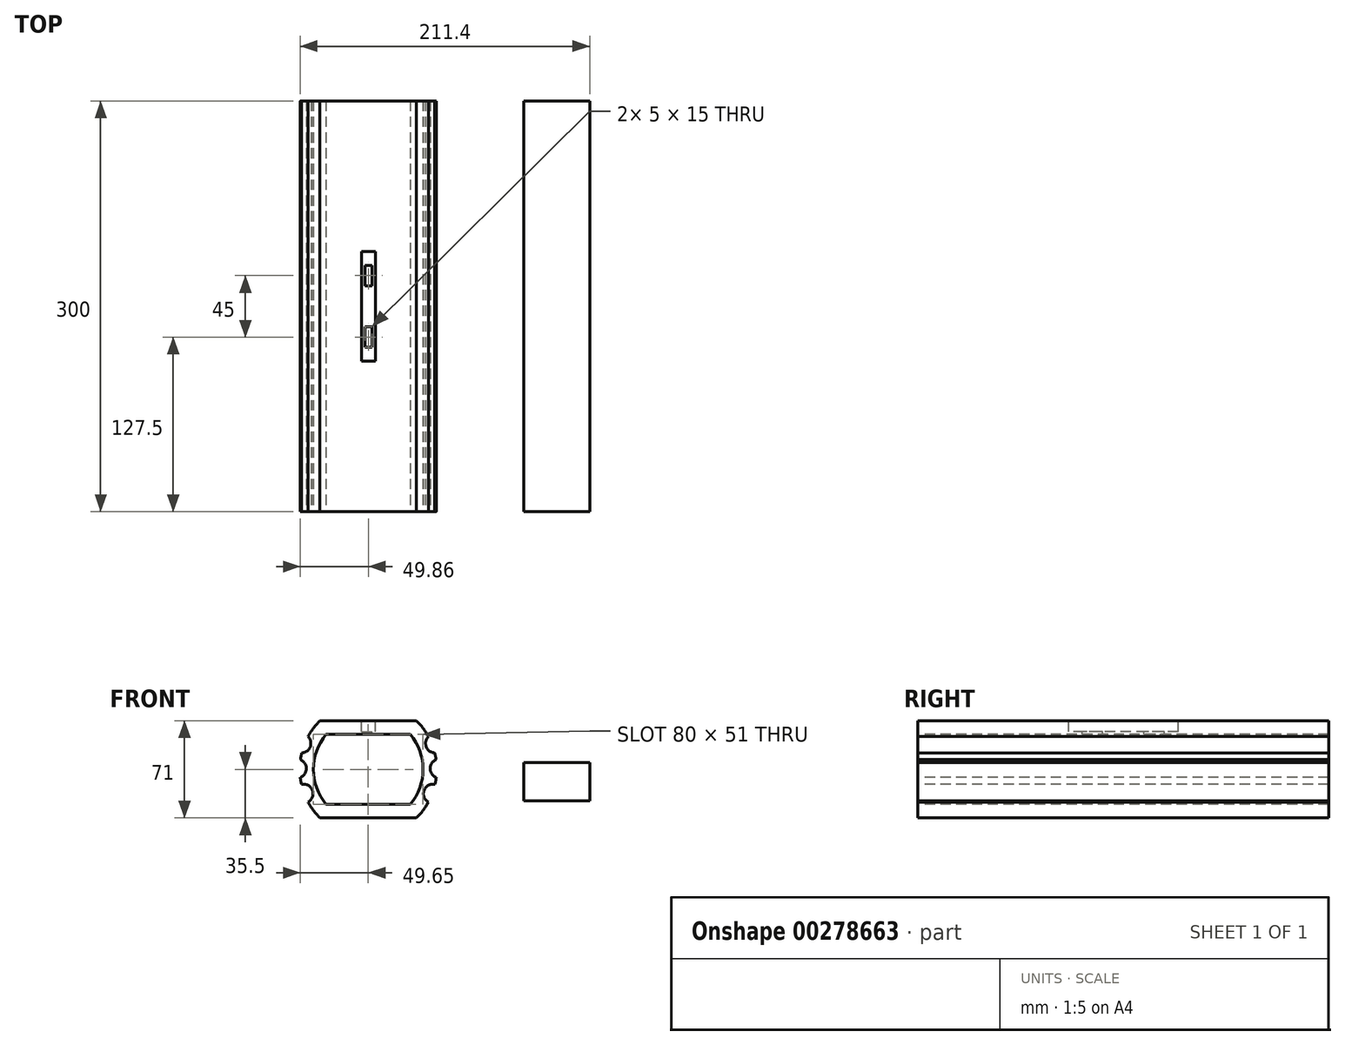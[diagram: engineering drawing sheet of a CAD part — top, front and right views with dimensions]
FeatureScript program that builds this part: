
annotation { "Feature Type Name" : "Feature", "Feature Type Description" : "" }
export const myFeature = defineFeature(function(context is Context, id is Id, definition is map)
    precondition{}
    {
        {
            var Q0;
            Q0=qCreatedBy(makeId("Front.planeOp"),FACE);
            var sketch = newSketch(context, id + "F0", { "sketchPlane" : qUnion([Q0])});
            skArc(sketch, "E0", {"start": v(-35.21, 35.5) * mm, "mid": v(-50, 0) * mm, "end": v(-35.21, -35.5) * mm});
            skLineSegment(sketch, "E1", {"start": v(-35.21, 35.5) * mm, "end": v(35.21, 35.5) * mm});
            skLineSegment(sketch, "E2", {"start": v(-35.21, -35.5) * mm, "end": v(35.21, -35.5) * mm});
            skArc(sketch, "E3.trimOffspring", {"start": v(35.21, -35.5) * mm, "mid": v(50, 0) * mm, "end": v(35.21, 35.5) * mm});
            skLineSegment(sketch, "E4.bottom", {"start": v(161.75, 4.82) * mm, "end": v(113.6, 4.82) * mm});
            skLineSegment(sketch, "E4.top", {"start": v(161.75, -22.95) * mm, "end": v(113.6, -22.95) * mm});
            skLineSegment(sketch, "E4.left", {"start": v(161.75, 4.82) * mm, "end": v(161.75, -22.95) * mm});
            skLineSegment(sketch, "E4.right", {"start": v(113.6, 4.82) * mm, "end": v(113.6, -22.95) * mm});
            skSolve(sketch);
        }
        {
            var Q0;
            Q0 = qSketchRegion(id + "F0", true);
            extrude(context, id + "F1", {"entities" : qUnion([Q0]), "depth" : 300 * mm});
        }
        {
            var Q0;
            Q0=makeQuery(id+"F1.opExtrude","CAP_FACE",FACE,{"disambiguationData":[OSD([sQuery(id+"F0.wireOp",EDGE,"E0"),sQuery(id+"F0.wireOp",EDGE,"E1"),sQuery(id+"F0.wireOp",EDGE,"E2"),sQuery(id+"F0.wireOp",EDGE,"E3.trimOffspring")])],"isStart":false});
            var sketch = newSketch(context, id + "F2", { "sketchPlane" : qUnion([Q0])});
            skArc(sketch, "E5", {"start": v(-30.82, 25.5) * mm, "mid": v(-40, 0) * mm, "end": v(-30.82, -25.5) * mm});
            skLineSegment(sketch, "E6", {"start": v(-30.82, 25.5) * mm, "end": v(30.82, 25.5) * mm});
            skLineSegment(sketch, "E7", {"start": v(-30.82, -25.5) * mm, "end": v(30.82, -25.5) * mm});
            skArc(sketch, "E8.trimOffspring", {"start": v(30.82, -25.5) * mm, "mid": v(40, 0) * mm, "end": v(30.82, 25.5) * mm});
            skSolve(sketch);
        }
        {
            var Q0;
            Q0 = qSketchRegion(id + "F2", true);
            extrude(context, id + "F3", {"entities" : qUnion([Q0]), "operationType" : NewBodyOperationType.REMOVE, "oppositeDirection" : true, "depth" : 300 * mm});
        }
        {
            var Q0;
            Q0=makeQuery(id+"F1.opExtrude","SWEPT_FACE",FACE,{"disambiguationData":[OSD([sQuery(id+"F0.wireOp",EDGE,"E1")])]});
            var sketch = newSketch(context, id + "F4", { "sketchPlane" : qUnion([Q0])});
            skLineSegment(sketch, "E9.bottom", {"start": v(-4.79, -110) * mm, "end": v(5.21, -110) * mm});
            skLineSegment(sketch, "E9.top", {"start": v(-4.79, -190) * mm, "end": v(5.21, -190) * mm});
            skLineSegment(sketch, "E9.left", {"start": v(-4.79, -110) * mm, "end": v(-4.79, -190) * mm});
            skLineSegment(sketch, "E9.right", {"start": v(5.21, -110) * mm, "end": v(5.21, -190) * mm});
            skSolve(sketch);
        }
        {
            var Q0;
            Q0 = qSketchRegion(id + "F4", true);
            extrude(context, id + "F5", {"entities" : qUnion([Q0]), "operationType" : NewBodyOperationType.REMOVE, "oppositeDirection" : true, "depth" : 8 * mm});
        }
        {
            var Q0;
            Q0=makeQuery(id+"F5.boolean.opBoolean","COPY",FACE,{"derivedFrom":makeQuery(id+"F5.opExtrude","CAP_FACE",FACE,{"disambiguationData":[OSD([sQuery(id+"F4.wireOp",EDGE,"E9.bottom"),sQuery(id+"F4.wireOp",EDGE,"E9.top"),sQuery(id+"F4.wireOp",EDGE,"E9.left"),sQuery(id+"F4.wireOp",EDGE,"E9.right")])],"isStart":false})});
            var sketch = newSketch(context, id + "F6", { "sketchPlane" : qUnion([Q0])});
            skLineSegment(sketch, "E10.bottom", {"start": v(-2.29, -120) * mm, "end": v(2.71, -120) * mm});
            skLineSegment(sketch, "E10.top", {"start": v(-2.29, -135) * mm, "end": v(2.71, -135) * mm});
            skLineSegment(sketch, "E10.left", {"start": v(-2.29, -120) * mm, "end": v(-2.29, -135) * mm});
            skLineSegment(sketch, "E10.right", {"start": v(2.71, -120) * mm, "end": v(2.71, -135) * mm});
            skLineSegment(sketch, "E11.bottom", {"start": v(-2.29, -165) * mm, "end": v(2.71, -165) * mm});
            skLineSegment(sketch, "E11.top", {"start": v(-2.29, -180) * mm, "end": v(2.71, -180) * mm});
            skLineSegment(sketch, "E11.left", {"start": v(-2.29, -165) * mm, "end": v(-2.29, -180) * mm});
            skLineSegment(sketch, "E11.right", {"start": v(2.71, -165) * mm, "end": v(2.71, -180) * mm});
            skSolve(sketch);
        }
        {
            var Q0;
            Q0 = qSketchRegion(id + "F6", true);
            extrude(context, id + "F7", {"entities" : qUnion([Q0]), "operationType" : NewBodyOperationType.REMOVE, "oppositeDirection" : true, "depth" : 5 * mm});
        }
        {
            var Q0;
            Q0=makeQuery(id+"F1.opExtrude","CAP_FACE",FACE,{"disambiguationData":[OSD([sQuery(id+"F0.wireOp",EDGE,"E0"),sQuery(id+"F0.wireOp",EDGE,"E1"),sQuery(id+"F0.wireOp",EDGE,"E2"),sQuery(id+"F0.wireOp",EDGE,"E3.trimOffspring")])],"isStart":false});
            var sketch = newSketch(context, id + "F8", { "sketchPlane" : qUnion([Q0])});
            skArc(sketch, "E12", {"start": v(43.92, 23.9) * mm, "mid": v(42.35, 16.43) * mm, "end": v(48.54, 11.97) * mm});
            skArc(sketch, "E13", {"start": v(49.5, 7.07) * mm, "mid": v(45.17, 0.51) * mm, "end": v(49.65, -5.94) * mm});
            skArc(sketch, "E14", {"start": v(48.79, -10.94) * mm, "mid": v(40.75, -15.31) * mm, "end": v(43.92, -23.9) * mm});
            skLineSegment(sketch, "E15", {"start": v(0, 45.54) * mm, "end": v(0, -53.5) * mm});
            skArc(sketch, "E16.MirrorCS", {"start": v(-43.92, 23.9) * mm, "mid": v(-42.35, 16.43) * mm, "end": v(-48.54, 11.97) * mm});
            skArc(sketch, "E17.MirrorCS", {"start": v(-49.5, 7.07) * mm, "mid": v(-45.17, 0.51) * mm, "end": v(-49.65, -5.94) * mm});
            skArc(sketch, "E18.MirrorCS", {"start": v(-48.79, -10.94) * mm, "mid": v(-40.75, -15.31) * mm, "end": v(-43.92, -23.9) * mm});
            skArc(sketch, "E19", {"start": v(48.54, 11.97) * mm, "mid": v(47.23, 18.33) * mm, "end": v(43.92, 23.9) * mm});
            skArc(sketch, "E20", {"start": v(49.65, -5.94) * mm, "mid": v(52.47, 0.6) * mm, "end": v(49.5, 7.07) * mm});
            skArc(sketch, "E21", {"start": v(43.92, -23.9) * mm, "mid": v(49.5, -18.6) * mm, "end": v(48.79, -10.94) * mm});
            skArc(sketch, "E22.MirrorCS", {"start": v(-48.54, 11.97) * mm, "mid": v(-47.23, 18.33) * mm, "end": v(-43.92, 23.9) * mm});
            skArc(sketch, "E23.MirrorCS", {"start": v(-49.65, -5.94) * mm, "mid": v(-52.47, 0.6) * mm, "end": v(-49.5, 7.07) * mm});
            skArc(sketch, "E24.MirrorCS", {"start": v(-43.92, -23.9) * mm, "mid": v(-49.5, -18.6) * mm, "end": v(-48.79, -10.94) * mm});
            skSolve(sketch);
        }
        {
            var Q0;
            Q0 = qSketchRegion(id + "F8", true);
            extrude(context, id + "F9", {"entities" : qUnion([Q0]), "operationType" : NewBodyOperationType.REMOVE, "oppositeDirection" : true, "depth" : 300 * mm});
        }
    });
